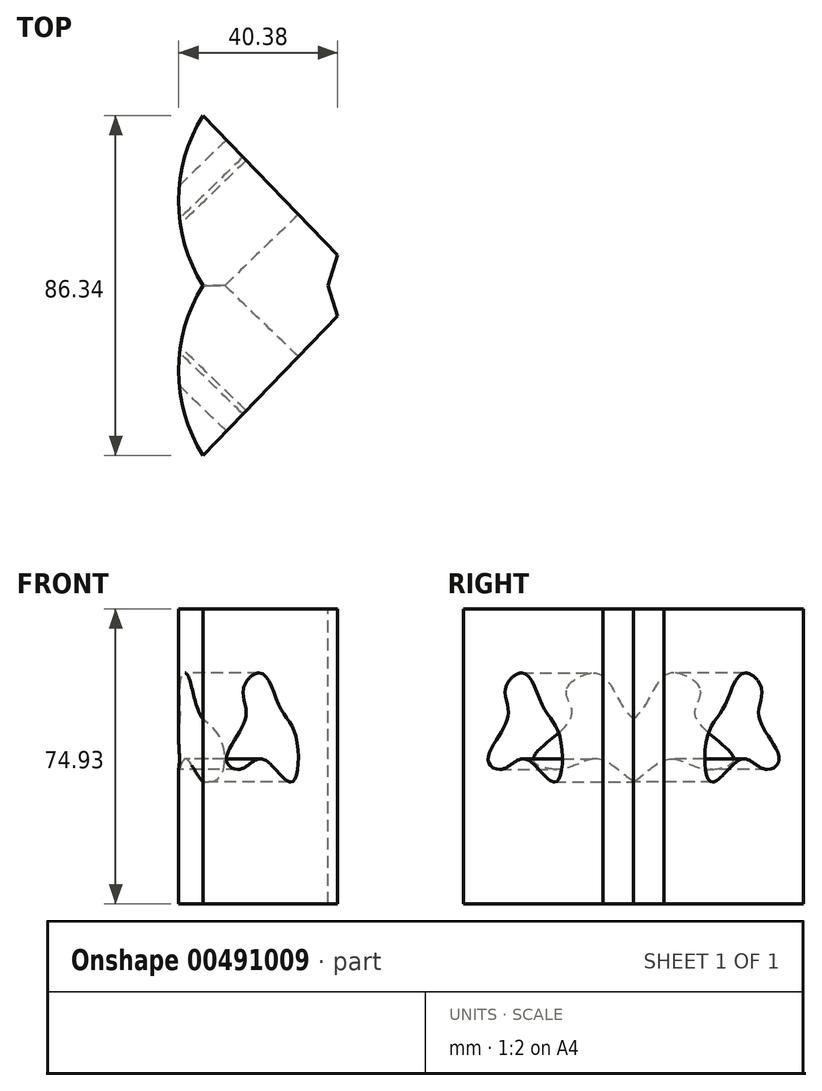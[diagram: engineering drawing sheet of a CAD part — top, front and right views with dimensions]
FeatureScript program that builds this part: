
annotation { "Feature Type Name" : "Feature", "Feature Type Description" : "" }
export const myFeature = defineFeature(function(context is Context, id is Id, definition is map)
    precondition{}
    {
        {
            var Q0;
            Q0=qCreatedBy(makeId("Top.planeOp"),FACE);
            var sketch = newSketch(context, id + "F0", { "sketchPlane" : qUnion([Q0])});
            skArc(sketch, "E0", {"start": v(0, 43.17) * mm, "mid": v(-6.13, 21.59) * mm, "end": v(0, 0) * mm});
            skLineSegment(sketch, "E1", {"start": v(0, 43.17) * mm, "end": v(34.25, 7.77) * mm});
            skLineSegment(sketch, "E2", {"start": v(34.25, 7.77) * mm, "end": v(21.87, -31.37) * mm});
            skLineSegment(sketch, "E3", {"start": v(21.87, -31.37) * mm, "end": v(21.87, -6.9) * mm});
            skLineSegment(sketch, "E4", {"start": v(21.87, -6.9) * mm, "end": v(0, 0) * mm});
            skSolve(sketch);
        }
        {
            var Q0;
            Q0 = qSketchRegion(id + "F0", true);
            extrude(context, id + "F1", {"entities" : qUnion([Q0]), "depth" : 74.93 * mm});
        }
        {
            var Q0;
            Q0=makeQuery(id+"F1.opExtrude","SWEPT_FACE",FACE,{"disambiguationData":[OSD([sQuery(id+"F0.wireOp",EDGE,"E1")])]});
            var sketch = newSketch(context, id + "F2", { "sketchPlane" : qUnion([Q0])});
            skFitSpline(sketch, "E5", {"points": [v(16.21, 54.79) * mm, v(9.54, 58.55) * mm, v(3.03, 50.17) * mm, v(-2.61, 43.32) * mm, v(-3.13, 32.54) * mm, v(0, 31.17) * mm, v(9.37, 36.82) * mm, v(17.24, 34.25) * mm, v(22.37, 36.3) * mm, v(18.43, 42.8) * mm, v(15.18, 48.97) * mm, v(16.21, 54.79) * mm]});
            skSolve(sketch);
        }
        {
            var Q0;
            Q0 = qSketchRegion(id + "F2", true);
            extrude(context, id + "F3", {"entities" : qUnion([Q0]), "operationType" : NewBodyOperationType.REMOVE, "oppositeDirection" : true, "depth" : 55.12 * mm});
        }
        {
            var Q0;
            Q0=qCreatedBy(makeId("Right.planeOp"),FACE);
            var sketch = newSketch(context, id + "F4", { "sketchPlane" : qUnion([Q0])});
            skLineSegment(sketch, "E6.bottom", {"start": v(-45.33, 85.17) * mm, "end": v(0, 85.17) * mm});
            skLineSegment(sketch, "E6.top", {"start": v(-45.33, 0) * mm, "end": v(0, 0) * mm});
            skLineSegment(sketch, "E6.left", {"start": v(-45.33, 85.17) * mm, "end": v(-45.33, 0) * mm});
            skLineSegment(sketch, "E6.right", {"start": v(0, 85.17) * mm, "end": v(0, 0) * mm});
            skSolve(sketch);
        }
        {
            var Q0;
            Q0 = qSketchRegion(id + "F4", true);
            extrude(context, id + "F5", {"entities" : qUnion([Q0]), "operationType" : NewBodyOperationType.REMOVE, "depth" : 70.87 * mm});
        }
        {
            var Q0;
            Q0=makeQuery(id+"F1.opExtrude","SWEPT_BODY",BODY,{"disambiguationData":[OSD([sQuery(id+"F0.wireOp",EDGE,"E0"),sQuery(id+"F0.wireOp",EDGE,"E1"),sQuery(id+"F0.wireOp",EDGE,"E2"),sQuery(id+"F0.wireOp",EDGE,"E3"),sQuery(id+"F0.wireOp",EDGE,"E4")])]});
            var Q1;
            Q1=qCreatedBy(makeId("Front.planeOp"),FACE);
            mirror(context, id + "F6", {"operationType" : NewBodyOperationType.ADD, "entities" : qUnion([Q0]), "mirrorPlane" : qUnion([Q1])});
        }
    });
